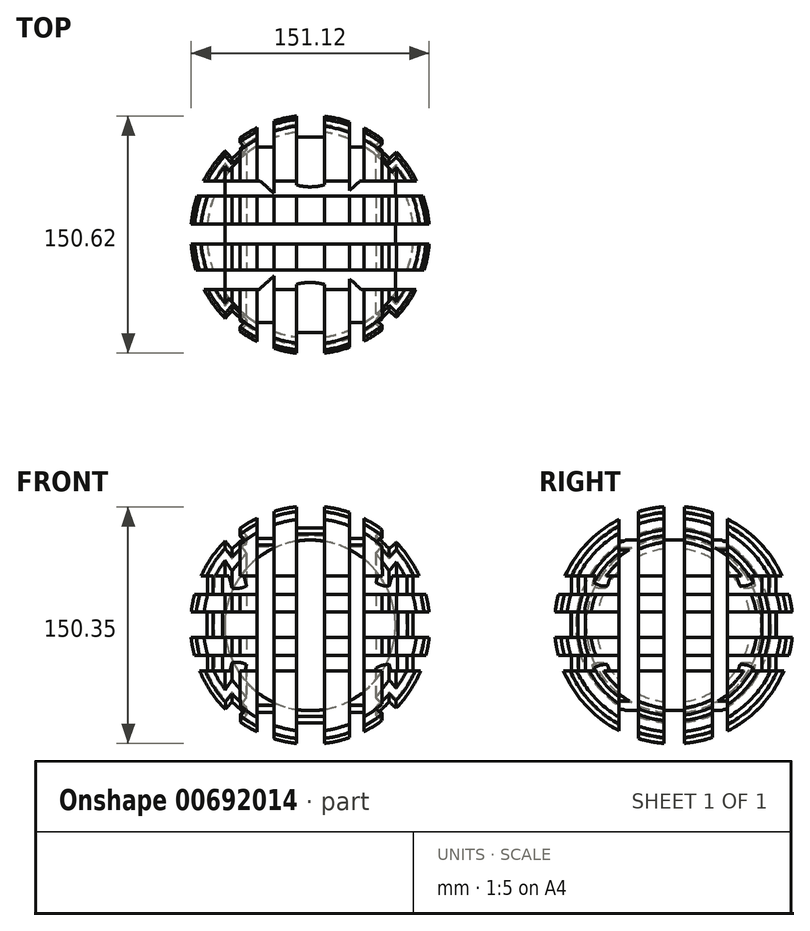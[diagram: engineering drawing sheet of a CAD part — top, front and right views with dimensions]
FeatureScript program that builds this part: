
annotation { "Feature Type Name" : "Feature", "Feature Type Description" : "" }
export const myFeature = defineFeature(function(context is Context, id is Id, definition is map)
    precondition{}
    {
        {
            var Q0;
            Q0=qCreatedBy(makeId("Front.planeOp"),FACE);
            var sketch = newSketch(context, id + "F0", { "sketchPlane" : qUnion([Q0])});
            skLineSegment(sketch, "E0", {"start": v(0, 78.83) * mm, "end": v(0, -79.53) * mm, "construction": true});
            skArc(sketch, "E1", {"start": v(0, 76.04) * mm, "mid": v(-76.23, 0.17) * mm, "end": v(0, -75.7) * mm});
            skLineSegment(sketch, "E2", {"start": v(0, 76.04) * mm, "end": v(0, -75.7) * mm});
            skSolve(sketch);
        }
        {
            var Q0;
            Q0 = qSketchRegion(id + "F0", true);
            var Q1;
            Q1=sQuery(id+"F0.wireOp",EDGE,"E2");
            revolve(context, id + "F1", {"entities" : qUnion([Q0]), "axis" : qUnion([Q1]), "revolveType" : RevolveType.FULL});
        }
        {
            var Q0;
            Q0=qCreatedBy(makeId("Front.planeOp"),FACE);
            var sketch = newSketch(context, id + "F2", { "sketchPlane" : qUnion([Q0])});
            skLineSegment(sketch, "E3.bottom", {"start": v(-8.65, 85.82) * mm, "end": v(9.13, 85.82) * mm});
            skLineSegment(sketch, "E3.top", {"start": v(-8.65, 62.11) * mm, "end": v(9.13, 62.11) * mm});
            skLineSegment(sketch, "E3.left", {"start": v(-8.65, 85.82) * mm, "end": v(-8.65, 62.11) * mm});
            skLineSegment(sketch, "E3.right", {"start": v(9.13, 85.82) * mm, "end": v(9.13, 62.11) * mm});
            skLineSegment(sketch, "E4", {"start": v(-115.26, 0) * mm, "end": v(92.45, 0) * mm, "construction": true});
            skSolve(sketch);
        }
        {
            var Q0;
            Q0 = qSketchRegion(id + "F2", true);
            var Q1;
            Q1=sQuery(id+"F2.wireOp",EDGE,"E4");
            revolve(context, id + "F3", {"operationType" : NewBodyOperationType.REMOVE, "entities" : qUnion([Q0]), "axis" : qUnion([Q1]), "revolveType" : RevolveType.FULL, "oppositeDirection" : true});
        }
        {
            var Q0;
            Q0=qCreatedBy(makeId("Front.planeOp"),FACE);
            var sketch = newSketch(context, id + "F4", { "sketchPlane" : qUnion([Q0])});
            skLineSegment(sketch, "E5.bottom", {"start": v(-81.33, 8.5) * mm, "end": v(-65.7, 8.5) * mm});
            skLineSegment(sketch, "E5.top", {"start": v(-81.33, -7.78) * mm, "end": v(-65.7, -7.78) * mm});
            skLineSegment(sketch, "E5.left", {"start": v(-81.33, 8.5) * mm, "end": v(-81.33, -7.78) * mm});
            skLineSegment(sketch, "E5.right", {"start": v(-65.7, 8.5) * mm, "end": v(-65.7, -7.78) * mm});
            skSolve(sketch);
        }
        {
            var Q0;
            Q0 = qSketchRegion(id + "F4", true);
            var Q1;
            Q1=sQuery(id+"F0.wireOp",EDGE,"E2");
            revolve(context, id + "F5", {"operationType" : NewBodyOperationType.REMOVE, "entities" : qUnion([Q0]), "axis" : qUnion([Q1]), "revolveType" : RevolveType.FULL, "oppositeDirection" : true});
        }
        {
            var Q0;
            Q0=qCreatedBy(makeId("Front.planeOp"),FACE);
            var sketch = newSketch(context, id + "F6", { "sketchPlane" : qUnion([Q0])});
            skLineSegment(sketch, "E6", {"start": v(-62.22, 62.81) * mm, "end": v(-49.64, 48.95) * mm});
            skLineSegment(sketch, "E7", {"start": v(-49.64, 48.95) * mm, "end": v(-40.4, 57.34) * mm});
            skLineSegment(sketch, "E8", {"start": v(-40.4, 57.34) * mm, "end": v(-52.92, 71.14) * mm});
            skLineSegment(sketch, "E9", {"start": v(-52.92, 71.14) * mm, "end": v(-62.22, 62.81) * mm});
            skLineSegment(sketch, "E10", {"start": v(41.76, 57.34) * mm, "end": v(56.96, 71.14) * mm});
            skLineSegment(sketch, "E11", {"start": v(56.96, 71.14) * mm, "end": v(65.48, 62.81) * mm});
            skLineSegment(sketch, "E12", {"start": v(65.48, 62.81) * mm, "end": v(50.2, 48.95) * mm});
            skLineSegment(sketch, "E13", {"start": v(50.2, 48.95) * mm, "end": v(41.76, 57.34) * mm});
            skLineSegment(sketch, "E14", {"start": v(-86.12, 0) * mm, "end": v(85.19, 0) * mm, "construction": true});
            skSolve(sketch);
        }
        {
            var Q0;
            Q0 = qSketchRegion(id + "F6", true);
            var Q1;
            Q1=sQuery(id+"F6.wireOp",EDGE,"E14");
            revolve(context, id + "F7", {"operationType" : NewBodyOperationType.REMOVE, "entities" : qUnion([Q0]), "axis" : qUnion([Q1]), "revolveType" : RevolveType.FULL, "oppositeDirection" : true});
        }
        {
            var Q0;
            Q0=qCreatedBy(makeId("Front.planeOp"),FACE);
            var sketch = newSketch(context, id + "F8", { "sketchPlane" : qUnion([Q0])});
            skLineSegment(sketch, "E15.bottom", {"start": v(76.44, 31.53) * mm, "end": v(65.55, 31.53) * mm});
            skLineSegment(sketch, "E15.top", {"start": v(76.44, 19.71) * mm, "end": v(65.55, 19.71) * mm});
            skLineSegment(sketch, "E15.left", {"start": v(76.44, 31.53) * mm, "end": v(76.44, 19.71) * mm});
            skLineSegment(sketch, "E15.right", {"start": v(65.55, 31.53) * mm, "end": v(65.55, 19.71) * mm});
            skLineSegment(sketch, "E16.bottom", {"start": v(76.44, -19.1) * mm, "end": v(65.55, -19.1) * mm});
            skLineSegment(sketch, "E16.top", {"start": v(76.44, -28.92) * mm, "end": v(65.55, -28.92) * mm});
            skLineSegment(sketch, "E16.left", {"start": v(76.44, -19.1) * mm, "end": v(76.44, -28.92) * mm});
            skLineSegment(sketch, "E16.right", {"start": v(65.55, -19.1) * mm, "end": v(65.55, -28.92) * mm});
            skLineSegment(sketch, "E17", {"start": v(0, 69.16) * mm, "end": v(0, -70.12) * mm});
            skLineSegment(sketch, "E18", {"start": v(0, 96.28) * mm, "end": v(0, -93.77) * mm, "construction": true});
            skSolve(sketch);
        }
        {
            var Q0;
            Q0 = qSketchRegion(id + "F8", true);
            var Q1;
            Q1=sQuery(id+"F8.wireOp",EDGE,"E17");
            revolve(context, id + "F9", {"operationType" : NewBodyOperationType.REMOVE, "entities" : qUnion([Q0]), "axis" : qUnion([Q1]), "revolveType" : RevolveType.FULL, "oppositeDirection" : true});
        }
        {
            var Q0;
            Q0=qCreatedBy(makeId("Top.planeOp"),FACE);
            var sketch = newSketch(context, id + "F10", { "sketchPlane" : qUnion([Q0])});
            skLineSegment(sketch, "E19.bottom", {"start": v(-80.74, 6.75) * mm, "end": v(-54.19, 6.75) * mm});
            skLineSegment(sketch, "E19.top", {"start": v(-80.74, -6.09) * mm, "end": v(-54.19, -6.09) * mm});
            skLineSegment(sketch, "E19.left", {"start": v(-80.74, 6.75) * mm, "end": v(-80.74, -6.09) * mm});
            skLineSegment(sketch, "E19.right", {"start": v(-54.19, 6.75) * mm, "end": v(-54.19, -6.09) * mm});
            skLineSegment(sketch, "E20.bottom", {"start": v(-80.74, 34.2) * mm, "end": v(-54.19, 34.2) * mm});
            skLineSegment(sketch, "E20.top", {"start": v(-80.74, 24.52) * mm, "end": v(-54.19, 24.52) * mm});
            skLineSegment(sketch, "E20.left", {"start": v(-80.74, 34.2) * mm, "end": v(-80.74, 24.52) * mm});
            skLineSegment(sketch, "E20.right", {"start": v(-54.19, 34.2) * mm, "end": v(-54.19, 24.52) * mm});
            skLineSegment(sketch, "E21.bottom", {"start": v(-80.74, -22.44) * mm, "end": v(-54.19, -22.44) * mm});
            skLineSegment(sketch, "E21.top", {"start": v(-80.74, -34.76) * mm, "end": v(-54.19, -34.76) * mm});
            skLineSegment(sketch, "E21.left", {"start": v(-80.74, -22.44) * mm, "end": v(-80.74, -34.76) * mm});
            skLineSegment(sketch, "E21.right", {"start": v(-54.19, -22.44) * mm, "end": v(-54.19, -34.76) * mm});
            skLineSegment(sketch, "E22", {"start": v(0, 78.87) * mm, "end": v(0, -78.02) * mm, "construction": true});
            skSolve(sketch);
        }
        {
            var Q0;
            Q0 = qSketchRegion(id + "F10", true);
            var Q1;
            Q1=sQuery(id+"F10.wireOp",EDGE,"E22");
            revolve(context, id + "F11", {"operationType" : NewBodyOperationType.REMOVE, "entities" : qUnion([Q0]), "axis" : qUnion([Q1]), "revolveType" : RevolveType.FULL, "oppositeDirection" : true});
        }
        {
            var Q0;
            Q0=qCreatedBy(makeId("Front.planeOp"),FACE);
            var sketch = newSketch(context, id + "F12", { "sketchPlane" : qUnion([Q0])});
            skLineSegment(sketch, "E23", {"start": v(-124.93, 0) * mm, "end": v(107.1, 0) * mm, "construction": true});
            skLineSegment(sketch, "E24.bottom", {"start": v(-33.66, 74.22) * mm, "end": v(-23.1, 74.22) * mm});
            skLineSegment(sketch, "E24.top", {"start": v(-33.66, 55.66) * mm, "end": v(-23.1, 55.66) * mm});
            skLineSegment(sketch, "E24.left", {"start": v(-33.66, 74.22) * mm, "end": v(-33.66, 55.66) * mm});
            skLineSegment(sketch, "E24.right", {"start": v(-23.1, 74.22) * mm, "end": v(-23.1, 55.66) * mm});
            skLineSegment(sketch, "E25.bottom", {"start": v(25.12, 74.22) * mm, "end": v(34.14, 74.22) * mm});
            skLineSegment(sketch, "E25.top", {"start": v(25.12, 55.66) * mm, "end": v(34.14, 55.66) * mm});
            skLineSegment(sketch, "E25.left", {"start": v(25.12, 74.22) * mm, "end": v(25.12, 55.66) * mm});
            skLineSegment(sketch, "E25.right", {"start": v(34.14, 74.22) * mm, "end": v(34.14, 55.66) * mm});
            skSolve(sketch);
        }
        {
            var Q0;
            Q0 = qSketchRegion(id + "F12", true);
            var Q1;
            Q1=sQuery(id+"F12.wireOp",EDGE,"E23");
            revolve(context, id + "F13", {"operationType" : NewBodyOperationType.REMOVE, "entities" : qUnion([Q0]), "axis" : qUnion([Q1]), "revolveType" : RevolveType.FULL, "oppositeDirection" : true});
        }
    });
